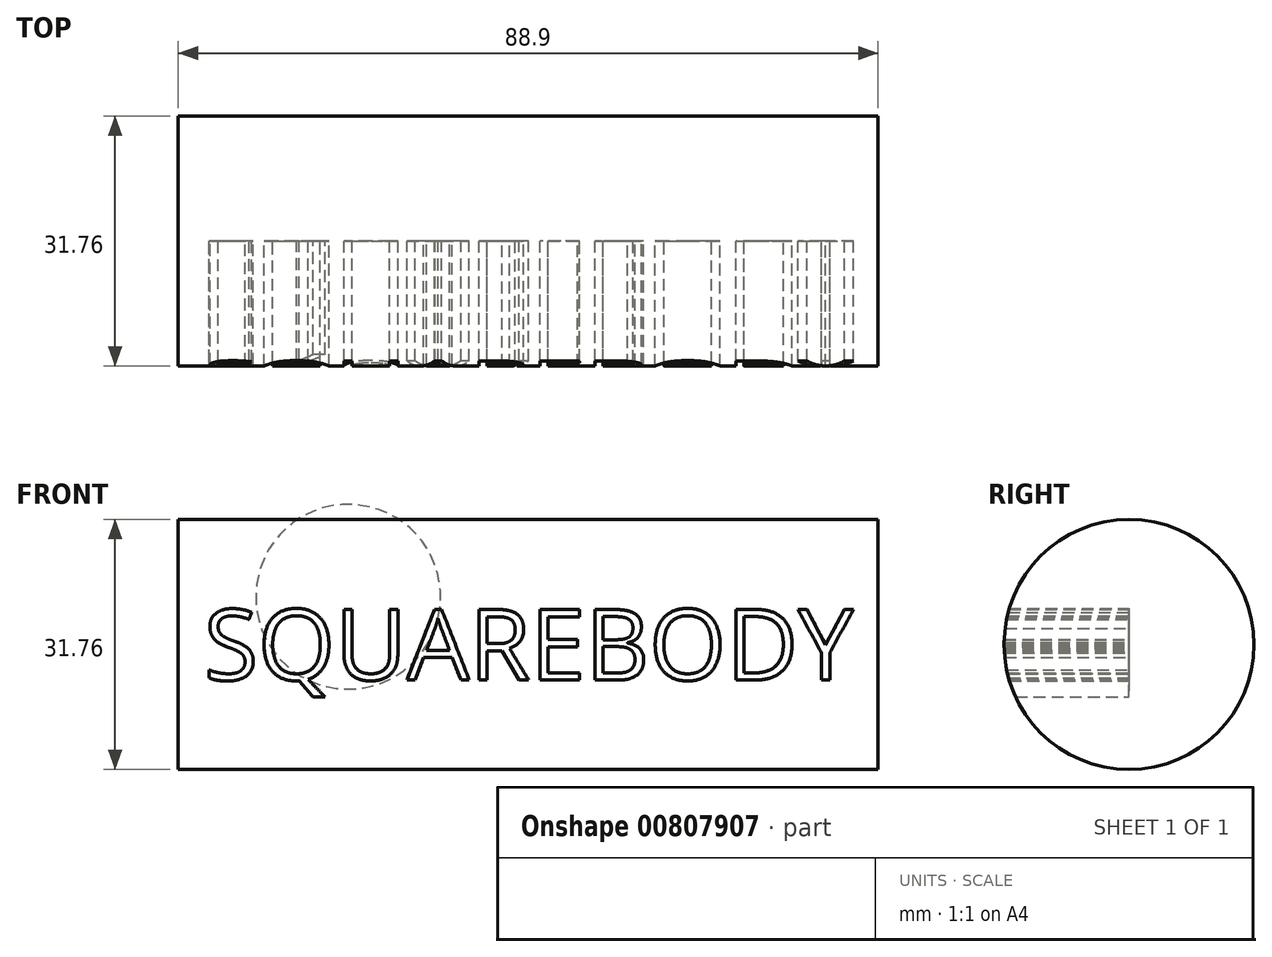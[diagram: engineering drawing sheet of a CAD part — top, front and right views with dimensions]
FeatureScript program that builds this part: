
annotation { "Feature Type Name" : "Feature", "Feature Type Description" : "" }
export const myFeature = defineFeature(function(context is Context, id is Id, definition is map)
    precondition{}
    {
        {
            var Q0;
            Q0=qCreatedBy(makeId("Right.planeOp"),FACE);
            var sketch = newSketch(context, id + "F0", { "sketchPlane" : qUnion([Q0])});
            skCircle(sketch, "E0", {"center": v(0, 0) * mm, "radius": 15.88 * mm});
            skSolve(sketch);
        }
        {
            var Q0;
            Q0=makeQuery(id+"F0.imprint","IMPRINT",FACE,{"disambiguationData":[TD([[makeQuery(id+"F0.imprint","IMPRINT",EDGE,{"derivedFrom":sQuery(id+"F0.wireOp",EDGE,"E0")}),1.0]])]});
            extrude(context, id + "F1", {"entities" : qUnion([Q0]), "depth" : 88.9 * mm, "offsetDistance" : 25.4 * mm});
        }
        {
            var Q0;
            Q0=qCreatedBy(makeId("Front.planeOp"),FACE);
            var sketch = newSketch(context, id + "F2", { "sketchPlane" : qUnion([Q0])});
            skText(sketch, "E1", { "text": " SQUAREBODY ", "fontName": "OpenSans-Regular.ttf"});
            skArc(sketch, "E2", {"start": v(2.57, 16.13) * mm, "mid": v(11.67, 13.5) * mm, "end": v(20.82, 15.95) * mm});
            skArc(sketch, "E3", {"start": v(20.82, 15.95) * mm, "mid": v(30.78, 13.39) * mm, "end": v(40.73, 15.95) * mm});
            skArc(sketch, "E4", {"start": v(40.73, 15.95) * mm, "mid": v(50.69, 13.27) * mm, "end": v(60.64, 15.95) * mm});
            skArc(sketch, "E5", {"start": v(60.64, 15.95) * mm, "mid": v(70.32, 13.5) * mm, "end": v(80, 15.95) * mm});
            const initialGuessF2  = {"E1": [0, -0.00451, 1, 0, 0.00903]};
            skSetInitialGuess(sketch, initialGuessF2);
            skSolve(sketch);
        }
        {
            var Q0;
            Q0 = qSketchRegion(id + "F2", true);
            extrude(context, id + "F3", {"entities" : qUnion([Q0]), "operationType" : NewBodyOperationType.REMOVE, "depth" : 58.17 * mm, "offsetDistance" : 25.4 * mm});
        }
    });
